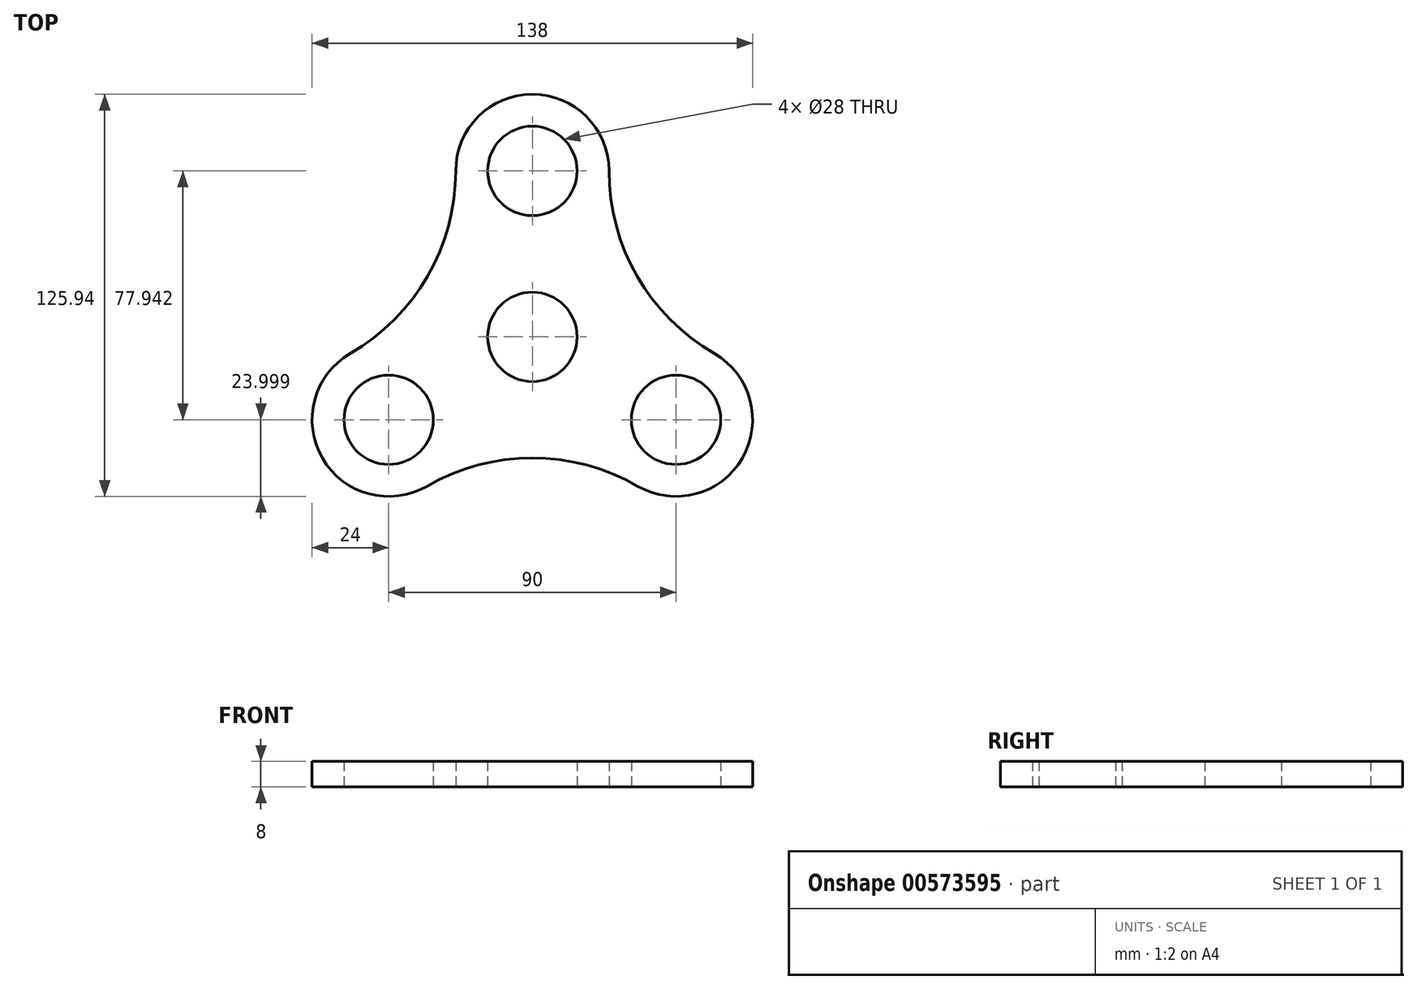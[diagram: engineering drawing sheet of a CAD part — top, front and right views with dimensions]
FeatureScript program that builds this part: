
annotation { "Feature Type Name" : "Feature", "Feature Type Description" : "" }
export const myFeature = defineFeature(function(context is Context, id is Id, definition is map)
    precondition{}
    {
        {
            var Q0;
            Q0=qCreatedBy(makeId("Top.planeOp"),FACE);
            var sketch = newSketch(context, id + "F0", { "sketchPlane" : qUnion([Q0])});
            skPoint(sketch, "E0.0.midPoint", {"position": v(22.5, 13) * mm});
            skCircle(sketch, "E1", {"center": v(0, 0) * mm, "radius": 14 * mm});
            skCircle(sketch, "E2", {"center": v(0, 51.96) * mm, "radius": 14 * mm});
            skCircle(sketch, "E3.1.0", {"center": v(-45, -25.98) * mm, "radius": 14 * mm});
            skCircle(sketch, "E3.2.0", {"center": v(45, -25.98) * mm, "radius": 14 * mm});
            skArc(sketch, "E4", {"start": v(24, 51.96) * mm, "mid": v(0, 75.96) * mm, "end": v(-24, 51.96) * mm});
            skArc(sketch, "E5.1.0", {"start": v(-57, -5.2) * mm, "mid": v(-65.78, -37.98) * mm, "end": v(-33, -46.77) * mm});
            skArc(sketch, "E5.2.0", {"start": v(33, -46.77) * mm, "mid": v(65.78, -37.98) * mm, "end": v(57, -5.2) * mm});
            skArc(sketch, "E6.trimOffspring", {"start": v(-57, -5.2) * mm, "mid": v(-32.84, 18.96) * mm, "end": v(-24, 51.96) * mm});
            skArc(sketch, "E7.1.0", {"start": v(33, -46.77) * mm, "mid": v(0, -37.92) * mm, "end": v(-33, -46.77) * mm});
            skArc(sketch, "E7.2.0", {"start": v(24, 51.96) * mm, "mid": v(32.84, 18.96) * mm, "end": v(57, -5.2) * mm});
            skSolve(sketch);
        }
        {
            var Q0;
            Q0 = qSketchRegion(id + "F0", true);
            extrude(context, id + "F1", {"entities" : qUnion([Q0]), "depth" : 8 * mm, "offsetDistance" : 25 * mm});
        }
    });
